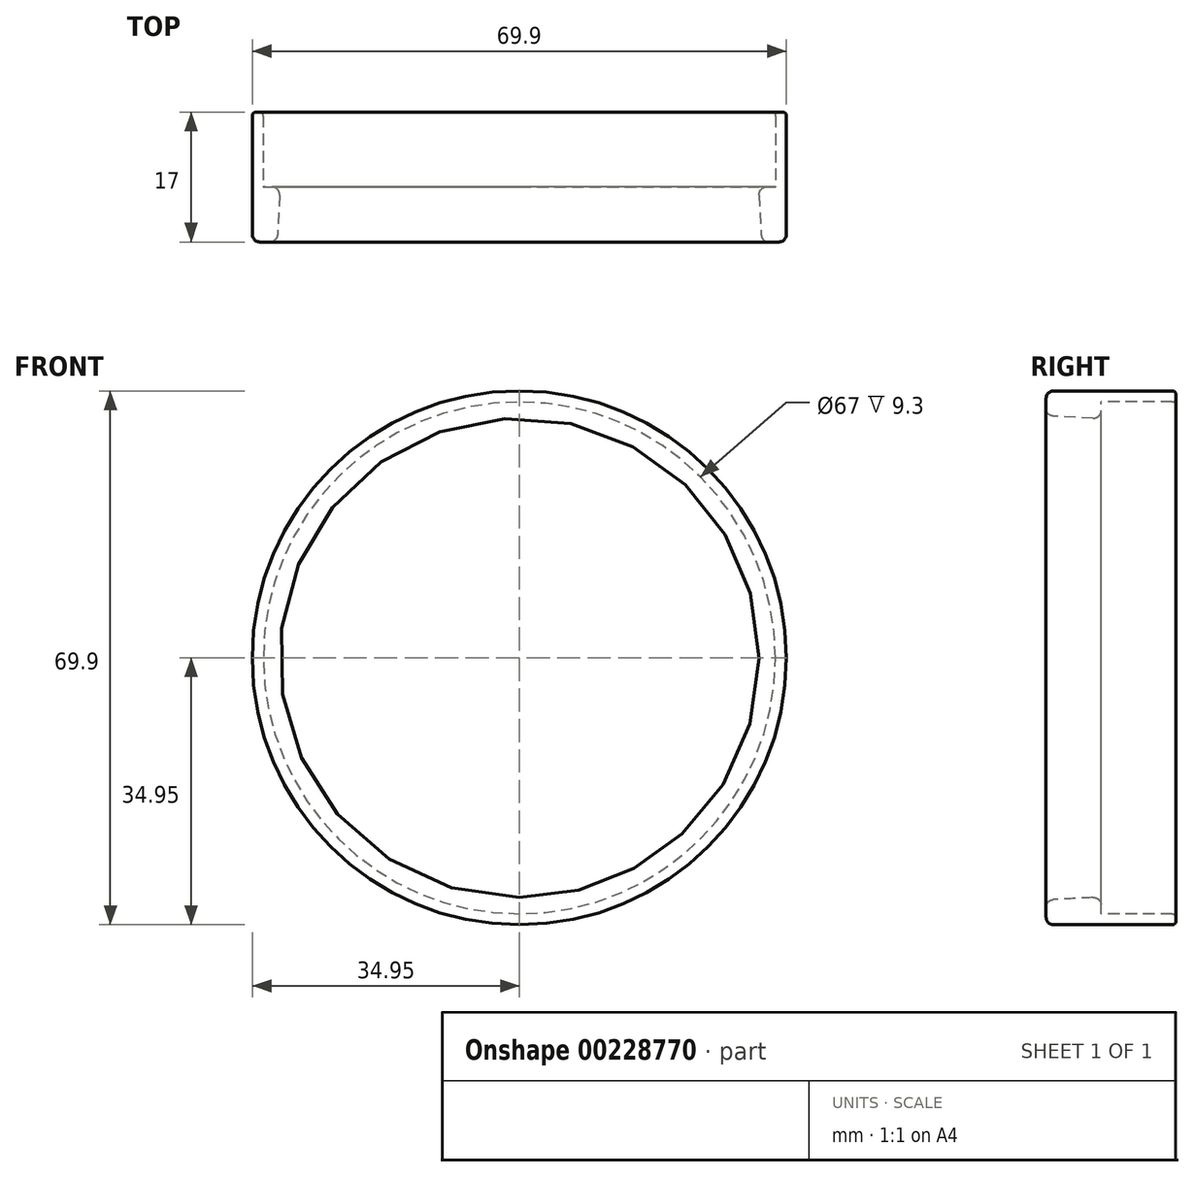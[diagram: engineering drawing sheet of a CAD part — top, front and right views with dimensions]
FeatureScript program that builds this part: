
annotation { "Feature Type Name" : "Feature", "Feature Type Description" : "" }
export const myFeature = defineFeature(function(context is Context, id is Id, definition is map)
    precondition{}
    {
        {
            var Q0;
            Q0=qCreatedBy(makeId("Right.planeOp"),FACE);
            var sketch = newSketch(context, id + "F0", { "sketchPlane" : qUnion([Q0])});
            skLineSegment(sketch, "E0.bottom", {"start": v(-7.5, 34.95) * mm, "end": v(8, 34.95) * mm});
            skLineSegment(sketch, "E0.left", {"start": v(-8.5, 33.95) * mm, "end": v(-8.5, 32.65) * mm});
            skLineSegment(sketch, "E0.right", {"start": v(8.5, 34.45) * mm, "end": v(8.5, 34) * mm});
            skPoint(sketch, "E0.middle", {"position": v(0, 33.5) * mm});
            skLineSegment(sketch, "E1", {"start": v(-1.3, 32.38) * mm, "end": v(-1.3, 33.5) * mm});
            skLineSegment(sketch, "E2", {"start": v(-1.3, 33.5) * mm, "end": v(8, 33.5) * mm});
            skPoint(sketch, "E3.orphan", {"position": v(8.5, 32.05) * mm});
            skLineSegment(sketch, "E4", {"start": v(-6.64, 0) * mm, "end": v(3.61, 0) * mm});
            skLineSegment(sketch, "E5", {"start": v(-2.35, 31.38) * mm, "end": v(-7.55, 31.65) * mm});
            skPoint(sketch, "E6.visualSharp", {"position": v(-8.5, 34.95) * mm});
            skArc(sketch, "E6.filletArc", {"start": v(-7.5, 34.95) * mm, "mid": v(-8.2, 34.66) * mm, "end": v(-8.5, 33.95) * mm});
            skPoint(sketch, "E7.visualSharp", {"position": v(-1.34, 31.32) * mm});
            skArc(sketch, "E7.filletArc", {"start": v(-2.35, 31.38) * mm, "mid": v(-1.61, 31.65) * mm, "end": v(-1.3, 32.38) * mm});
            skPoint(sketch, "E8.visualSharp", {"position": v(-8.5, 31.7) * mm});
            skArc(sketch, "E8.filletArc", {"start": v(-8.5, 32.65) * mm, "mid": v(-8.23, 31.96) * mm, "end": v(-7.55, 31.65) * mm});
            skPoint(sketch, "E9.visualSharp", {"position": v(8.5, 33.5) * mm});
            skArc(sketch, "E9.filletArc", {"start": v(8, 33.5) * mm, "mid": v(8.35, 33.65) * mm, "end": v(8.5, 34) * mm});
            skPoint(sketch, "E10.visualSharp", {"position": v(8.5, 34.95) * mm});
            skArc(sketch, "E10.filletArc", {"start": v(8.5, 34.45) * mm, "mid": v(8.35, 34.8) * mm, "end": v(8, 34.95) * mm});
            skSolve(sketch);
        }
        {
            var Q0;
            Q0=makeQuery(id+"F0.imprint","IMPRINT",FACE,{"disambiguationData":[TD([[makeQuery(id+"F0.imprint","IMPRINT",EDGE,{"derivedFrom":sQuery(id+"F0.wireOp",EDGE,"E0.bottom")}),-1.0]])]});
            var Q1;
            Q1=sQuery(id+"F0.wireOp",EDGE,"E4");
            revolve(context, id + "F1", {"entities" : qUnion([Q0]), "axis" : qUnion([Q1]), "revolveType" : RevolveType.FULL});
        }
    });
